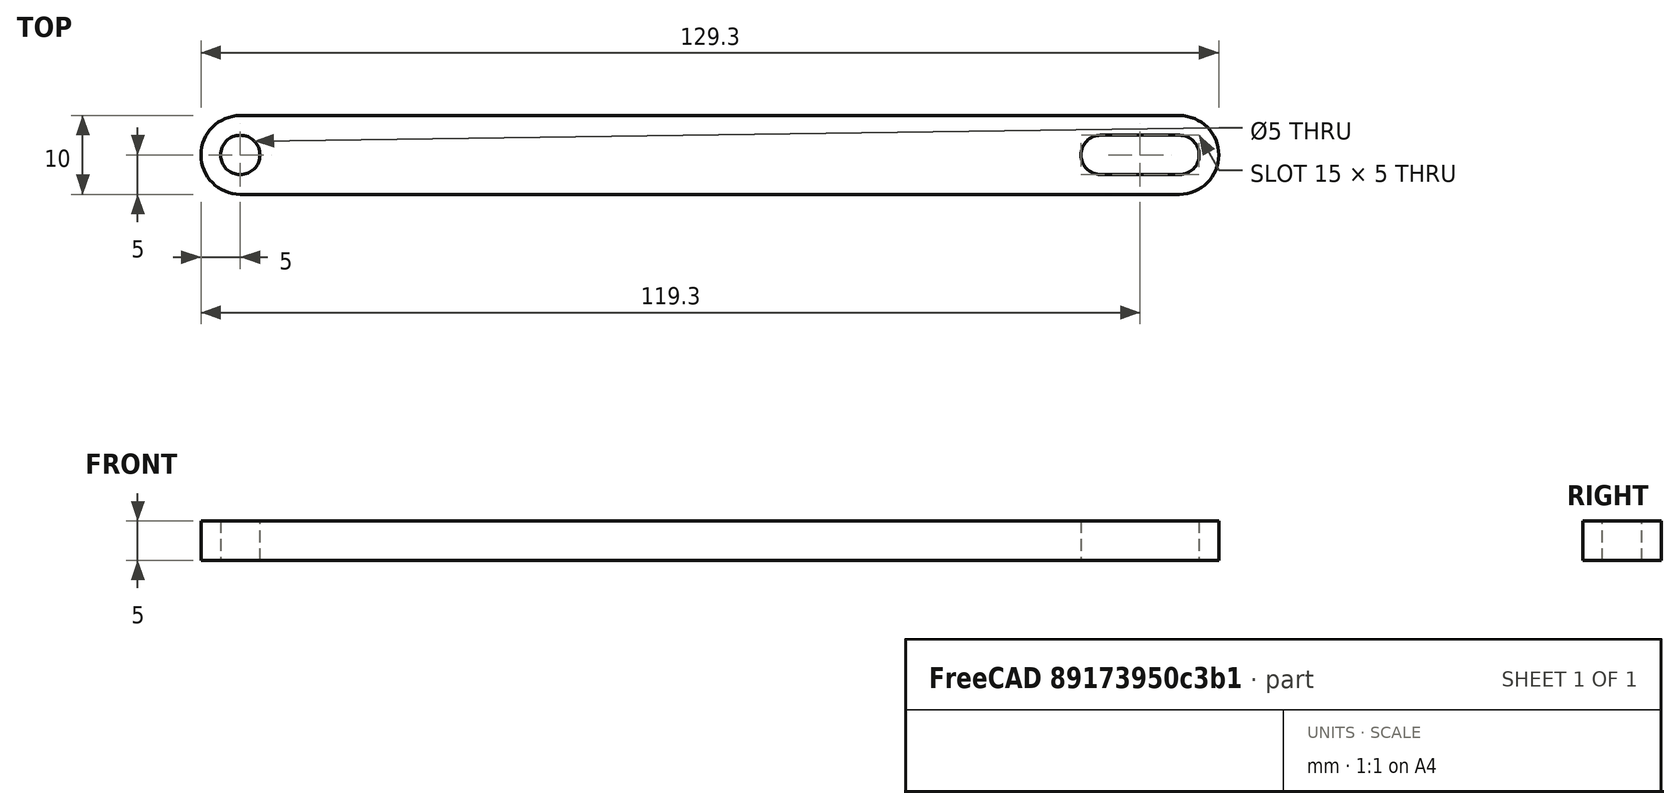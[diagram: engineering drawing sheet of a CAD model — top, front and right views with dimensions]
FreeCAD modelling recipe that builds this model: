
FCSTD DOCUMENT  (FreeCAD 0.19R24276 (Git))
Label: test_arm1
License: All rights reserved
LicenseURL: http://en.wikipedia.org/wiki/All_rights_reserved
objects: Sketcher::SketchObject×1, PartDesign::Pad×1, PartDesign::Body×1
note: 4 computed .brp shape members not serialized (recipe doc carries the construction recipe); baked Part::Feature solids carry a one-line shape summary decoded from their .brp

FEATURE [Sketcher::SketchObject] Sketch
  FullyConstrained = true
  MapMode = 5
  Support = -> [XY_Plane]
  sketch-geometry (12):
    g0: LineSegment StartX=0 StartY=0 StartZ=0 EndX=119.3 EndY=0 EndZ=0
    g1: Circle CenterX=0 CenterY=0 CenterZ=0 NormalX=0 NormalY=0 NormalZ=1 AngleXU=0 Radius=2.5
    g2: ArcOfCircle CenterX=0 CenterY=0 CenterZ=0 NormalX=0 NormalY=0 NormalZ=1 AngleXU=0 Radius=5 StartAngle=1.5708 EndAngle=4.71239
    g3: ArcOfCircle CenterX=119.3 CenterY=0 CenterZ=0 NormalX=0 NormalY=0 NormalZ=1 AngleXU=0 Radius=5 StartAngle=4.71239 EndAngle=7.85398
    g4: LineSegment StartX=-3.31477e-11 StartY=-5 StartZ=0 EndX=119.3 EndY=-5 EndZ=0
    g5: LineSegment StartX=-3.31032e-11 StartY=5 StartZ=0 EndX=119.3 EndY=5 EndZ=0
    g6: ArcOfCircle CenterX=109.3 CenterY=2e-16 CenterZ=0 NormalX=0 NormalY=0 NormalZ=1 AngleXU=0 Radius=2.5 StartAngle=1.5708 EndAngle=4.71239
    g7: ArcOfCircle CenterX=119.3 CenterY=0 CenterZ=0 NormalX=0 NormalY=0 NormalZ=1 AngleXU=0 Radius=2.5 StartAngle=4.71239 EndAngle=7.85398
    g8: LineSegment StartX=109.3 StartY=-2.5 StartZ=0 EndX=119.3 EndY=-2.5 EndZ=0
    g9: LineSegment StartX=109.3 StartY=2.5 StartZ=0 EndX=119.3 EndY=2.5 EndZ=0
    g10: LineSegment StartX=109.3 StartY=2e-16 StartZ=0 EndX=119.3 EndY=0 EndZ=0
    g11: LineSegment StartX=109.3 StartY=2e-16 StartZ=0 EndX=114.3 EndY=1e-16 EndZ=0
  constraints (27):
    c: Coincident(g0,g-1)
    c: PointOnObject(g0,g-1)
    c: Coincident(g1,g-1)
    c: Diameter(g1) = 5
    c: Tangent(g2,g5) = 1.5708
    c: Tangent(g2,g4) = -1.5708
    c: Tangent(g4,g3) = -1.5708
    c: Tangent(g5,g3) = 1.5708
    c: Horizontal(g4)
    c: Coincident(g2,g1)
    c: DistanceY(g3,g3) = 10
    c: Tangent(g6,g9) = 1.5708
    c: Tangent(g6,g8) = -1.5708
    c: Tangent(g8,g7) = -1.5708
    c: Tangent(g9,g7) = 1.5708
    c: Horizontal(g8)
    c: Equal(g6,g7)
    c: DistanceY(g7,g7) = 5
    c: Coincident(g10,g6)
    c: Coincident(g10,g7)
    c: DistanceX(g10,g10) = 10
    c: Coincident(g11,g6)
    c: PointOnObject(g11,g10)
    c: DistanceX(g6,g11) = 5
    c: Coincident(g0,g3)
    c: Coincident(g7,g3)
    c: DistanceX(g1,g11) = 114.3
FEATURE [PartDesign::Pad] Pad
  Direction = (1,1,1)
  Length = 5
  Length2 = 100
  Profile = -> Sketch
  Type = 0
FEATURE [PartDesign::Body] Body
  Group = -> [Sketch,Pad]
  Origin = -> Origin
  Tip = -> Pad
